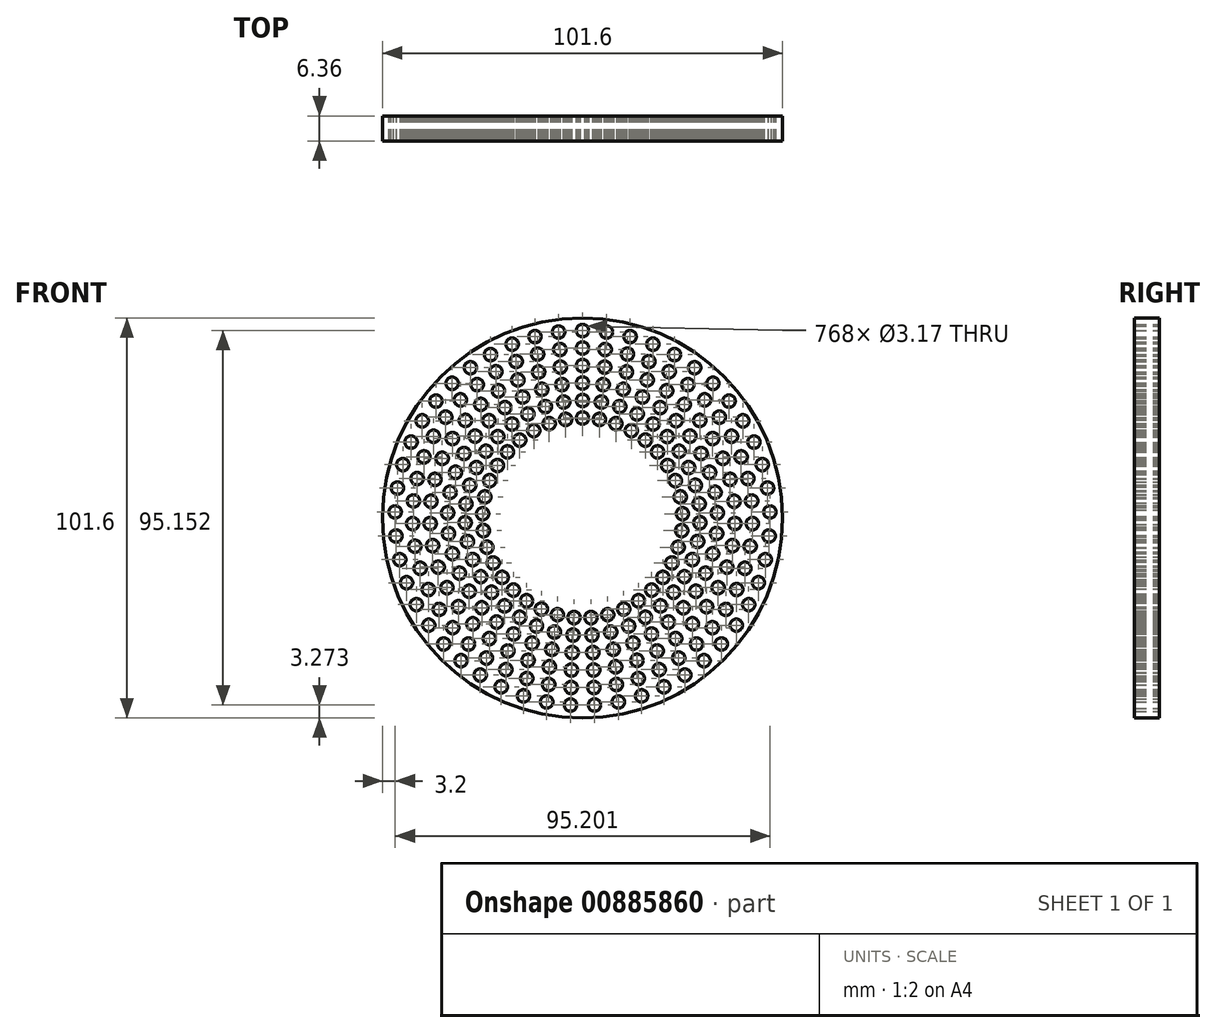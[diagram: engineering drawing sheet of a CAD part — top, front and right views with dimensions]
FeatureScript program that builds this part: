
annotation { "Feature Type Name" : "Feature", "Feature Type Description" : "" }
export const myFeature = defineFeature(function(context is Context, id is Id, definition is map)
    precondition{}
    {
        {
            var Q0;
            Q0=qCreatedBy(makeId("Front.planeOp"),FACE);
            var sketch = newSketch(context, id + "F0", { "sketchPlane" : qUnion([Q0])});
            skCircle(sketch, "E0", {"center": v(0, 0) * mm, "radius": 50.8 * mm});
            skCircle(sketch, "E1", {"center": v(0, 47.63) * mm, "radius": 1.59 * mm});
            skCircle(sketch, "E2.1.0", {"center": v(-6.1, 47.23) * mm, "radius": 1.59 * mm});
            skCircle(sketch, "E2.2.0", {"center": v(-12.08, 46.07) * mm, "radius": 1.59 * mm});
            skCircle(sketch, "E2.3.0", {"center": v(-17.87, 44.14) * mm, "radius": 1.59 * mm});
            skCircle(sketch, "E2.4.0", {"center": v(-23.37, 41.5) * mm, "radius": 1.59 * mm});
            skCircle(sketch, "E2.5.0", {"center": v(-28.49, 38.17) * mm, "radius": 1.59 * mm});
            skCircle(sketch, "E2.6.0", {"center": v(-33.13, 34.21) * mm, "radius": 1.59 * mm});
            skCircle(sketch, "E2.7.0", {"center": v(-37.23, 29.7) * mm, "radius": 1.59 * mm});
            skCircle(sketch, "E2.8.0", {"center": v(-40.73, 24.69) * mm, "radius": 1.59 * mm});
            skCircle(sketch, "E2.9.0", {"center": v(-43.55, 19.28) * mm, "radius": 1.59 * mm});
            skCircle(sketch, "E2.10.0", {"center": v(-45.66, 13.55) * mm, "radius": 1.59 * mm});
            skCircle(sketch, "E2.11.0", {"center": v(-47.01, 7.6) * mm, "radius": 1.59 * mm});
            skCircle(sketch, "E2.12.0", {"center": v(-47.6, 1.53) * mm, "radius": 1.59 * mm});
            skCircle(sketch, "E2.13.0", {"center": v(-47.4, -4.57) * mm, "radius": 1.59 * mm});
            skCircle(sketch, "E2.14.0", {"center": v(-46.43, -10.6) * mm, "radius": 1.59 * mm});
            skCircle(sketch, "E2.15.0", {"center": v(-44.7, -16.45) * mm, "radius": 1.59 * mm});
            skCircle(sketch, "E2.16.0", {"center": v(-42.22, -22.03) * mm, "radius": 1.59 * mm});
            skCircle(sketch, "E2.17.0", {"center": v(-39.06, -27.25) * mm, "radius": 1.59 * mm});
            skCircle(sketch, "E2.18.0", {"center": v(-35.26, -32.02) * mm, "radius": 1.59 * mm});
            skCircle(sketch, "E2.19.0", {"center": v(-30.87, -36.26) * mm, "radius": 1.59 * mm});
            skCircle(sketch, "E2.20.0", {"center": v(-25.98, -39.91) * mm, "radius": 1.59 * mm});
            skCircle(sketch, "E2.21.0", {"center": v(-20.66, -42.9) * mm, "radius": 1.59 * mm});
            skCircle(sketch, "E2.22.0", {"center": v(-15, -45.2) * mm, "radius": 1.59 * mm});
            skCircle(sketch, "E2.23.0", {"center": v(-9.1, -46.75) * mm, "radius": 1.59 * mm});
            skCircle(sketch, "E2.24.0", {"center": v(-3.05, -47.53) * mm, "radius": 1.59 * mm});
            skCircle(sketch, "E2.25.0", {"center": v(3.05, -47.53) * mm, "radius": 1.59 * mm});
            skCircle(sketch, "E2.26.0", {"center": v(9.1, -46.75) * mm, "radius": 1.59 * mm});
            skCircle(sketch, "E2.27.0", {"center": v(15, -45.2) * mm, "radius": 1.59 * mm});
            skCircle(sketch, "E2.28.0", {"center": v(20.66, -42.9) * mm, "radius": 1.59 * mm});
            skCircle(sketch, "E2.29.0", {"center": v(25.98, -39.91) * mm, "radius": 1.59 * mm});
            skCircle(sketch, "E2.30.0", {"center": v(30.87, -36.26) * mm, "radius": 1.59 * mm});
            skCircle(sketch, "E2.31.0", {"center": v(35.26, -32.02) * mm, "radius": 1.59 * mm});
            skCircle(sketch, "E2.32.0", {"center": v(39.06, -27.25) * mm, "radius": 1.59 * mm});
            skCircle(sketch, "E2.33.0", {"center": v(42.22, -22.03) * mm, "radius": 1.59 * mm});
            skCircle(sketch, "E2.34.0", {"center": v(44.7, -16.45) * mm, "radius": 1.59 * mm});
            skCircle(sketch, "E2.35.0", {"center": v(46.43, -10.6) * mm, "radius": 1.59 * mm});
            skCircle(sketch, "E2.36.0", {"center": v(47.4, -4.57) * mm, "radius": 1.59 * mm});
            skCircle(sketch, "E2.37.0", {"center": v(47.6, 1.53) * mm, "radius": 1.59 * mm});
            skCircle(sketch, "E2.38.0", {"center": v(47.01, 7.6) * mm, "radius": 1.59 * mm});
            skCircle(sketch, "E2.39.0", {"center": v(45.66, 13.55) * mm, "radius": 1.59 * mm});
            skCircle(sketch, "E2.40.0", {"center": v(43.55, 19.28) * mm, "radius": 1.59 * mm});
            skCircle(sketch, "E3", {"center": v(0, 43.18) * mm, "radius": 1.59 * mm});
            skCircle(sketch, "E4.1.0", {"center": v(-5.76, 42.8) * mm, "radius": 1.59 * mm});
            skCircle(sketch, "E4.2.0", {"center": v(-11.4, 41.65) * mm, "radius": 1.59 * mm});
            skCircle(sketch, "E4.3.0", {"center": v(-16.86, 39.75) * mm, "radius": 1.59 * mm});
            skCircle(sketch, "E4.4.0", {"center": v(-22, 37.15) * mm, "radius": 1.59 * mm});
            skCircle(sketch, "E4.5.0", {"center": v(-26.76, 33.89) * mm, "radius": 1.59 * mm});
            skCircle(sketch, "E4.6.0", {"center": v(-31.04, 30.02) * mm, "radius": 1.59 * mm});
            skCircle(sketch, "E4.7.0", {"center": v(-34.76, 25.61) * mm, "radius": 1.59 * mm});
            skCircle(sketch, "E4.8.0", {"center": v(-37.87, 20.75) * mm, "radius": 1.59 * mm});
            skCircle(sketch, "E4.9.0", {"center": v(-40.3, 15.52) * mm, "radius": 1.59 * mm});
            skCircle(sketch, "E4.10.0", {"center": v(-42, 10) * mm, "radius": 1.59 * mm});
            skCircle(sketch, "E4.11.0", {"center": v(-42.96, 4.32) * mm, "radius": 1.59 * mm});
            skCircle(sketch, "E4.12.0", {"center": v(-43.16, -1.44) * mm, "radius": 1.59 * mm});
            skCircle(sketch, "E4.13.0", {"center": v(-42.58, -7.18) * mm, "radius": 1.59 * mm});
            skCircle(sketch, "E4.14.0", {"center": v(-41.24, -12.8) * mm, "radius": 1.59 * mm});
            skCircle(sketch, "E4.15.0", {"center": v(-39.17, -18.18) * mm, "radius": 1.59 * mm});
            skCircle(sketch, "E4.16.0", {"center": v(-36.4, -23.23) * mm, "radius": 1.59 * mm});
            skCircle(sketch, "E4.17.0", {"center": v(-32.97, -27.88) * mm, "radius": 1.59 * mm});
            skCircle(sketch, "E4.18.0", {"center": v(-28.96, -32.02) * mm, "radius": 1.59 * mm});
            skCircle(sketch, "E4.19.0", {"center": v(-24.44, -35.6) * mm, "radius": 1.59 * mm});
            skCircle(sketch, "E4.20.0", {"center": v(-19.47, -38.54) * mm, "radius": 1.59 * mm});
            skCircle(sketch, "E4.21.0", {"center": v(-14.16, -40.8) * mm, "radius": 1.59 * mm});
            skCircle(sketch, "E4.22.0", {"center": v(-8.6, -42.31) * mm, "radius": 1.59 * mm});
            skCircle(sketch, "E4.23.0", {"center": v(-2.88, -43.08) * mm, "radius": 1.59 * mm});
            skCircle(sketch, "E4.24.0", {"center": v(2.88, -43.08) * mm, "radius": 1.59 * mm});
            skCircle(sketch, "E4.25.0", {"center": v(8.6, -42.31) * mm, "radius": 1.59 * mm});
            skCircle(sketch, "E4.26.0", {"center": v(14.16, -40.8) * mm, "radius": 1.59 * mm});
            skCircle(sketch, "E4.27.0", {"center": v(19.47, -38.54) * mm, "radius": 1.59 * mm});
            skCircle(sketch, "E4.28.0", {"center": v(24.44, -35.6) * mm, "radius": 1.59 * mm});
            skCircle(sketch, "E4.29.0", {"center": v(28.96, -32.02) * mm, "radius": 1.59 * mm});
            skCircle(sketch, "E4.30.0", {"center": v(32.97, -27.88) * mm, "radius": 1.59 * mm});
            skCircle(sketch, "E4.31.0", {"center": v(36.4, -23.23) * mm, "radius": 1.59 * mm});
            skCircle(sketch, "E4.32.0", {"center": v(39.17, -18.18) * mm, "radius": 1.59 * mm});
            skCircle(sketch, "E4.33.0", {"center": v(41.24, -12.8) * mm, "radius": 1.59 * mm});
            skCircle(sketch, "E4.34.0", {"center": v(42.58, -7.18) * mm, "radius": 1.59 * mm});
            skCircle(sketch, "E4.35.0", {"center": v(43.16, -1.44) * mm, "radius": 1.59 * mm});
            skCircle(sketch, "E4.36.0", {"center": v(42.96, 4.32) * mm, "radius": 1.59 * mm});
            skCircle(sketch, "E4.37.0", {"center": v(42, 10) * mm, "radius": 1.59 * mm});
            skCircle(sketch, "E4.38.0", {"center": v(40.3, 15.52) * mm, "radius": 1.59 * mm});
            skCircle(sketch, "E5.1.41.0", {"center": v(40.73, 24.69) * mm, "radius": 1.59 * mm});
            skCircle(sketch, "E5.1.42.0", {"center": v(37.23, 29.7) * mm, "radius": 1.59 * mm});
            skCircle(sketch, "E5.1.43.0", {"center": v(33.13, 34.21) * mm, "radius": 1.59 * mm});
            skCircle(sketch, "E5.1.44.0", {"center": v(28.49, 38.17) * mm, "radius": 1.59 * mm});
            skCircle(sketch, "E5.1.45.0", {"center": v(23.37, 41.5) * mm, "radius": 1.59 * mm});
            skCircle(sketch, "E5.1.46.0", {"center": v(17.87, 44.14) * mm, "radius": 1.59 * mm});
            skCircle(sketch, "E5.1.47.0", {"center": v(12.08, 46.07) * mm, "radius": 1.59 * mm});
            skCircle(sketch, "E5.1.48.0", {"center": v(6.1, 47.23) * mm, "radius": 1.59 * mm});
            skCircle(sketch, "E6.1.39.0", {"center": v(37.87, 20.75) * mm, "radius": 1.59 * mm});
            skCircle(sketch, "E6.1.40.0", {"center": v(34.76, 25.61) * mm, "radius": 1.59 * mm});
            skCircle(sketch, "E6.1.41.0", {"center": v(31.04, 30.02) * mm, "radius": 1.59 * mm});
            skCircle(sketch, "E6.1.42.0", {"center": v(26.76, 33.89) * mm, "radius": 1.59 * mm});
            skCircle(sketch, "E6.1.43.0", {"center": v(22, 37.15) * mm, "radius": 1.59 * mm});
            skCircle(sketch, "E6.1.44.0", {"center": v(16.86, 39.75) * mm, "radius": 1.59 * mm});
            skCircle(sketch, "E6.1.45.0", {"center": v(11.4, 41.65) * mm, "radius": 1.59 * mm});
            skCircle(sketch, "E6.1.46.0", {"center": v(5.76, 42.8) * mm, "radius": 1.59 * mm});
            skCircle(sketch, "E7", {"center": v(0, 38.74) * mm, "radius": 1.59 * mm});
            skCircle(sketch, "E8.1.0", {"center": v(-5.64, 38.32) * mm, "radius": 1.59 * mm});
            skCircle(sketch, "E8.2.0", {"center": v(-11.16, 37.1) * mm, "radius": 1.59 * mm});
            skCircle(sketch, "E8.3.0", {"center": v(-16.44, 35.07) * mm, "radius": 1.59 * mm});
            skCircle(sketch, "E8.4.0", {"center": v(-21.37, 32.3) * mm, "radius": 1.59 * mm});
            skCircle(sketch, "E8.5.0", {"center": v(-25.85, 28.85) * mm, "radius": 1.59 * mm});
            skCircle(sketch, "E8.6.0", {"center": v(-29.77, 24.78) * mm, "radius": 1.59 * mm});
            skCircle(sketch, "E8.7.0", {"center": v(-33.06, 20.18) * mm, "radius": 1.59 * mm});
            skCircle(sketch, "E8.8.0", {"center": v(-35.65, 15.15) * mm, "radius": 1.59 * mm});
            skCircle(sketch, "E8.9.0", {"center": v(-37.48, 9.8) * mm, "radius": 1.59 * mm});
            skCircle(sketch, "E8.10.0", {"center": v(-38.5, 4.24) * mm, "radius": 1.59 * mm});
            skCircle(sketch, "E8.11.0", {"center": v(-38.7, -1.41) * mm, "radius": 1.59 * mm});
            skCircle(sketch, "E8.12.0", {"center": v(-38.1, -7.04) * mm, "radius": 1.59 * mm});
            skCircle(sketch, "E8.13.0", {"center": v(-36.66, -12.5) * mm, "radius": 1.59 * mm});
            skCircle(sketch, "E8.14.0", {"center": v(-34.45, -17.71) * mm, "radius": 1.59 * mm});
            skCircle(sketch, "E8.15.0", {"center": v(-31.5, -22.54) * mm, "radius": 1.59 * mm});
            skCircle(sketch, "E8.16.0", {"center": v(-27.89, -26.88) * mm, "radius": 1.59 * mm});
            skCircle(sketch, "E8.17.0", {"center": v(-23.67, -30.66) * mm, "radius": 1.59 * mm});
            skCircle(sketch, "E8.18.0", {"center": v(-18.96, -33.78) * mm, "radius": 1.59 * mm});
            skCircle(sketch, "E8.19.0", {"center": v(-13.84, -36.18) * mm, "radius": 1.59 * mm});
            skCircle(sketch, "E8.20.0", {"center": v(-8.42, -37.8) * mm, "radius": 1.59 * mm});
            skCircle(sketch, "E8.21.0", {"center": v(-2.83, -38.63) * mm, "radius": 1.59 * mm});
            skCircle(sketch, "E8.22.0", {"center": v(2.83, -38.63) * mm, "radius": 1.59 * mm});
            skCircle(sketch, "E8.23.0", {"center": v(8.42, -37.8) * mm, "radius": 1.59 * mm});
            skCircle(sketch, "E8.24.0", {"center": v(13.84, -36.18) * mm, "radius": 1.59 * mm});
            skCircle(sketch, "E8.25.0", {"center": v(18.96, -33.78) * mm, "radius": 1.59 * mm});
            skCircle(sketch, "E8.26.0", {"center": v(23.67, -30.66) * mm, "radius": 1.59 * mm});
            skCircle(sketch, "E8.27.0", {"center": v(27.89, -26.88) * mm, "radius": 1.59 * mm});
            skCircle(sketch, "E8.28.0", {"center": v(31.5, -22.54) * mm, "radius": 1.59 * mm});
            skCircle(sketch, "E8.29.0", {"center": v(34.45, -17.71) * mm, "radius": 1.59 * mm});
            skCircle(sketch, "E8.30.0", {"center": v(36.66, -12.5) * mm, "radius": 1.59 * mm});
            skCircle(sketch, "E8.31.0", {"center": v(38.1, -7.04) * mm, "radius": 1.59 * mm});
            skCircle(sketch, "E8.32.0", {"center": v(38.7, -1.41) * mm, "radius": 1.59 * mm});
            skCircle(sketch, "E8.33.0", {"center": v(38.5, 4.24) * mm, "radius": 1.59 * mm});
            skCircle(sketch, "E8.34.0", {"center": v(37.48, 9.8) * mm, "radius": 1.59 * mm});
            skCircle(sketch, "E8.35.0", {"center": v(35.65, 15.15) * mm, "radius": 1.59 * mm});
            skCircle(sketch, "E8.36.0", {"center": v(33.06, 20.18) * mm, "radius": 1.59 * mm});
            skCircle(sketch, "E8.37.0", {"center": v(29.77, 24.78) * mm, "radius": 1.59 * mm});
            skCircle(sketch, "E8.38.0", {"center": v(25.85, 28.85) * mm, "radius": 1.59 * mm});
            skCircle(sketch, "E8.39.0", {"center": v(21.37, 32.3) * mm, "radius": 1.59 * mm});
            skCircle(sketch, "E8.40.0", {"center": v(16.44, 35.07) * mm, "radius": 1.59 * mm});
            skCircle(sketch, "E8.41.0", {"center": v(11.16, 37.1) * mm, "radius": 1.59 * mm});
            skCircle(sketch, "E8.42.0", {"center": v(5.64, 38.32) * mm, "radius": 1.59 * mm});
            skCircle(sketch, "E9", {"center": v(0, 34.3) * mm, "radius": 1.59 * mm});
            skCircle(sketch, "E10.1.0", {"center": v(-5.23, 33.89) * mm, "radius": 1.59 * mm});
            skCircle(sketch, "E10.2.0", {"center": v(-10.35, 32.7) * mm, "radius": 1.59 * mm});
            skCircle(sketch, "E10.3.0", {"center": v(-15.22, 30.73) * mm, "radius": 1.59 * mm});
            skCircle(sketch, "E10.4.0", {"center": v(-19.73, 28.05) * mm, "radius": 1.59 * mm});
            skCircle(sketch, "E10.5.0", {"center": v(-23.78, 24.7) * mm, "radius": 1.59 * mm});
            skCircle(sketch, "E10.6.0", {"center": v(-27.27, 20.79) * mm, "radius": 1.59 * mm});
            skCircle(sketch, "E10.7.0", {"center": v(-30.12, 16.38) * mm, "radius": 1.59 * mm});
            skCircle(sketch, "E10.8.0", {"center": v(-32.27, 11.6) * mm, "radius": 1.59 * mm});
            skCircle(sketch, "E10.9.0", {"center": v(-33.66, 6.53) * mm, "radius": 1.59 * mm});
            skCircle(sketch, "E10.10.0", {"center": v(-34.26, 1.31) * mm, "radius": 1.59 * mm});
            skCircle(sketch, "E10.11.0", {"center": v(-34.06, -3.93) * mm, "radius": 1.59 * mm});
            skCircle(sketch, "E10.12.0", {"center": v(-33.06, -9.09) * mm, "radius": 1.59 * mm});
            skCircle(sketch, "E10.13.0", {"center": v(-31.29, -14.03) * mm, "radius": 1.59 * mm});
            skCircle(sketch, "E10.14.0", {"center": v(-28.78, -18.64) * mm, "radius": 1.59 * mm});
            skCircle(sketch, "E10.15.0", {"center": v(-25.6, -22.81) * mm, "radius": 1.59 * mm});
            skCircle(sketch, "E10.16.0", {"center": v(-21.82, -26.45) * mm, "radius": 1.59 * mm});
            skCircle(sketch, "E10.17.0", {"center": v(-17.52, -29.47) * mm, "radius": 1.59 * mm});
            skCircle(sketch, "E10.18.0", {"center": v(-12.82, -31.8) * mm, "radius": 1.59 * mm});
            skCircle(sketch, "E10.19.0", {"center": v(-7.81, -33.39) * mm, "radius": 1.59 * mm});
            skCircle(sketch, "E10.20.0", {"center": v(-2.62, -34.19) * mm, "radius": 1.59 * mm});
            skCircle(sketch, "E10.21.0", {"center": v(2.62, -34.19) * mm, "radius": 1.59 * mm});
            skCircle(sketch, "E10.22.0", {"center": v(7.81, -33.39) * mm, "radius": 1.59 * mm});
            skCircle(sketch, "E10.23.0", {"center": v(12.82, -31.8) * mm, "radius": 1.59 * mm});
            skCircle(sketch, "E10.24.0", {"center": v(17.52, -29.47) * mm, "radius": 1.59 * mm});
            skCircle(sketch, "E10.25.0", {"center": v(21.82, -26.45) * mm, "radius": 1.59 * mm});
            skCircle(sketch, "E10.26.0", {"center": v(25.6, -22.81) * mm, "radius": 1.59 * mm});
            skCircle(sketch, "E10.27.0", {"center": v(28.78, -18.64) * mm, "radius": 1.59 * mm});
            skCircle(sketch, "E10.28.0", {"center": v(31.29, -14.03) * mm, "radius": 1.59 * mm});
            skCircle(sketch, "E10.29.0", {"center": v(33.06, -9.09) * mm, "radius": 1.59 * mm});
            skCircle(sketch, "E10.30.0", {"center": v(34.06, -3.93) * mm, "radius": 1.59 * mm});
            skCircle(sketch, "E10.31.0", {"center": v(34.26, 1.31) * mm, "radius": 1.59 * mm});
            skCircle(sketch, "E10.32.0", {"center": v(33.66, 6.53) * mm, "radius": 1.59 * mm});
            skCircle(sketch, "E10.33.0", {"center": v(32.27, 11.6) * mm, "radius": 1.59 * mm});
            skCircle(sketch, "E10.34.0", {"center": v(30.12, 16.38) * mm, "radius": 1.59 * mm});
            skCircle(sketch, "E10.35.0", {"center": v(27.27, 20.79) * mm, "radius": 1.59 * mm});
            skCircle(sketch, "E10.36.0", {"center": v(23.78, 24.7) * mm, "radius": 1.59 * mm});
            skCircle(sketch, "E10.37.0", {"center": v(19.73, 28.05) * mm, "radius": 1.59 * mm});
            skCircle(sketch, "E10.38.0", {"center": v(15.22, 30.73) * mm, "radius": 1.59 * mm});
            skCircle(sketch, "E10.39.0", {"center": v(10.35, 32.7) * mm, "radius": 1.59 * mm});
            skCircle(sketch, "E10.40.0", {"center": v(5.23, 33.89) * mm, "radius": 1.59 * mm});
            skCircle(sketch, "E11", {"center": v(0, 29.85) * mm, "radius": 1.59 * mm});
            skCircle(sketch, "E12.1.0", {"center": v(-4.79, 29.46) * mm, "radius": 1.59 * mm});
            skCircle(sketch, "E12.2.0", {"center": v(-9.45, 28.3) * mm, "radius": 1.59 * mm});
            skCircle(sketch, "E12.3.0", {"center": v(-13.87, 26.43) * mm, "radius": 1.59 * mm});
            skCircle(sketch, "E12.4.0", {"center": v(-17.93, 23.86) * mm, "radius": 1.59 * mm});
            skCircle(sketch, "E12.5.0", {"center": v(-21.52, 20.67) * mm, "radius": 1.59 * mm});
            skCircle(sketch, "E12.6.0", {"center": v(-24.56, 16.95) * mm, "radius": 1.59 * mm});
            skCircle(sketch, "E12.7.0", {"center": v(-26.96, 12.8) * mm, "radius": 1.59 * mm});
            skCircle(sketch, "E12.8.0", {"center": v(-28.67, 8.3) * mm, "radius": 1.59 * mm});
            skCircle(sketch, "E12.9.0", {"center": v(-29.63, 3.6) * mm, "radius": 1.59 * mm});
            skCircle(sketch, "E12.10.0", {"center": v(-29.82, -1.2) * mm, "radius": 1.59 * mm});
            skCircle(sketch, "E12.11.0", {"center": v(-29.24, -5.97) * mm, "radius": 1.59 * mm});
            skCircle(sketch, "E12.12.0", {"center": v(-27.9, -10.58) * mm, "radius": 1.59 * mm});
            skCircle(sketch, "E12.13.0", {"center": v(-25.85, -14.92) * mm, "radius": 1.59 * mm});
            skCircle(sketch, "E12.14.0", {"center": v(-23.12, -18.88) * mm, "radius": 1.59 * mm});
            skCircle(sketch, "E12.15.0", {"center": v(-19.8, -22.34) * mm, "radius": 1.59 * mm});
            skCircle(sketch, "E12.16.0", {"center": v(-15.95, -25.22) * mm, "radius": 1.59 * mm});
            skCircle(sketch, "E12.17.0", {"center": v(-11.7, -27.46) * mm, "radius": 1.59 * mm});
            skCircle(sketch, "E12.18.0", {"center": v(-7.14, -28.98) * mm, "radius": 1.59 * mm});
            skCircle(sketch, "E12.19.0", {"center": v(-2.4, -29.75) * mm, "radius": 1.59 * mm});
            skCircle(sketch, "E12.20.0", {"center": v(2.4, -29.75) * mm, "radius": 1.59 * mm});
            skCircle(sketch, "E12.21.0", {"center": v(7.14, -28.98) * mm, "radius": 1.59 * mm});
            skCircle(sketch, "E12.22.0", {"center": v(11.7, -27.46) * mm, "radius": 1.59 * mm});
            skCircle(sketch, "E12.23.0", {"center": v(15.95, -25.22) * mm, "radius": 1.59 * mm});
            skCircle(sketch, "E12.24.0", {"center": v(19.8, -22.34) * mm, "radius": 1.59 * mm});
            skCircle(sketch, "E12.25.0", {"center": v(23.12, -18.88) * mm, "radius": 1.59 * mm});
            skCircle(sketch, "E12.26.0", {"center": v(25.85, -14.92) * mm, "radius": 1.59 * mm});
            skCircle(sketch, "E12.27.0", {"center": v(27.9, -10.58) * mm, "radius": 1.59 * mm});
            skCircle(sketch, "E12.28.0", {"center": v(29.24, -5.97) * mm, "radius": 1.59 * mm});
            skCircle(sketch, "E12.29.0", {"center": v(29.82, -1.2) * mm, "radius": 1.59 * mm});
            skCircle(sketch, "E12.30.0", {"center": v(29.63, 3.6) * mm, "radius": 1.59 * mm});
            skCircle(sketch, "E12.31.0", {"center": v(28.67, 8.3) * mm, "radius": 1.59 * mm});
            skCircle(sketch, "E12.32.0", {"center": v(26.96, 12.8) * mm, "radius": 1.59 * mm});
            skCircle(sketch, "E12.33.0", {"center": v(24.56, 16.95) * mm, "radius": 1.59 * mm});
            skCircle(sketch, "E12.34.0", {"center": v(21.52, 20.67) * mm, "radius": 1.59 * mm});
            skCircle(sketch, "E12.35.0", {"center": v(17.93, 23.86) * mm, "radius": 1.59 * mm});
            skCircle(sketch, "E12.36.0", {"center": v(13.87, 26.43) * mm, "radius": 1.59 * mm});
            skCircle(sketch, "E12.37.0", {"center": v(9.45, 28.3) * mm, "radius": 1.59 * mm});
            skCircle(sketch, "E12.38.0", {"center": v(4.79, 29.46) * mm, "radius": 1.59 * mm});
            skCircle(sketch, "E13", {"center": v(0, 25.4) * mm, "radius": 1.59 * mm});
            skCircle(sketch, "E14.1.0", {"center": v(-4.3, 25.03) * mm, "radius": 1.59 * mm});
            skCircle(sketch, "E14.2.0", {"center": v(-8.46, 23.95) * mm, "radius": 1.59 * mm});
            skCircle(sketch, "E14.3.0", {"center": v(-12.39, 22.17) * mm, "radius": 1.59 * mm});
            skCircle(sketch, "E14.4.0", {"center": v(-15.96, 19.76) * mm, "radius": 1.59 * mm});
            skCircle(sketch, "E14.5.0", {"center": v(-19.07, 16.78) * mm, "radius": 1.59 * mm});
            skCircle(sketch, "E14.6.0", {"center": v(-21.63, 13.32) * mm, "radius": 1.59 * mm});
            skCircle(sketch, "E14.7.0", {"center": v(-23.57, 9.47) * mm, "radius": 1.59 * mm});
            skCircle(sketch, "E14.8.0", {"center": v(-24.83, 5.35) * mm, "radius": 1.59 * mm});
            skCircle(sketch, "E14.9.0", {"center": v(-25.38, 1.08) * mm, "radius": 1.59 * mm});
            skCircle(sketch, "E14.10.0", {"center": v(-25.2, -3.23) * mm, "radius": 1.59 * mm});
            skCircle(sketch, "E14.11.0", {"center": v(-24.29, -7.44) * mm, "radius": 1.59 * mm});
            skCircle(sketch, "E14.12.0", {"center": v(-22.68, -11.44) * mm, "radius": 1.59 * mm});
            skCircle(sketch, "E14.13.0", {"center": v(-20.42, -15.1) * mm, "radius": 1.59 * mm});
            skCircle(sketch, "E14.14.0", {"center": v(-17.58, -18.34) * mm, "radius": 1.59 * mm});
            skCircle(sketch, "E14.15.0", {"center": v(-14.22, -21.04) * mm, "radius": 1.59 * mm});
            skCircle(sketch, "E14.16.0", {"center": v(-10.46, -23.15) * mm, "radius": 1.59 * mm});
            skCircle(sketch, "E14.17.0", {"center": v(-6.4, -24.58) * mm, "radius": 1.59 * mm});
            skCircle(sketch, "E14.18.0", {"center": v(-2.15, -25.3) * mm, "radius": 1.59 * mm});
            skCircle(sketch, "E14.19.0", {"center": v(2.15, -25.3) * mm, "radius": 1.59 * mm});
            skCircle(sketch, "E14.20.0", {"center": v(6.4, -24.58) * mm, "radius": 1.59 * mm});
            skCircle(sketch, "E14.21.0", {"center": v(10.46, -23.15) * mm, "radius": 1.59 * mm});
            skCircle(sketch, "E14.22.0", {"center": v(14.22, -21.04) * mm, "radius": 1.59 * mm});
            skCircle(sketch, "E14.23.0", {"center": v(17.58, -18.34) * mm, "radius": 1.59 * mm});
            skCircle(sketch, "E14.24.0", {"center": v(20.42, -15.1) * mm, "radius": 1.59 * mm});
            skCircle(sketch, "E14.25.0", {"center": v(22.68, -11.44) * mm, "radius": 1.59 * mm});
            skCircle(sketch, "E14.26.0", {"center": v(24.29, -7.44) * mm, "radius": 1.59 * mm});
            skCircle(sketch, "E14.27.0", {"center": v(25.2, -3.23) * mm, "radius": 1.59 * mm});
            skCircle(sketch, "E14.28.0", {"center": v(25.38, 1.08) * mm, "radius": 1.59 * mm});
            skCircle(sketch, "E14.29.0", {"center": v(24.83, 5.35) * mm, "radius": 1.59 * mm});
            skCircle(sketch, "E14.30.0", {"center": v(23.57, 9.47) * mm, "radius": 1.59 * mm});
            skCircle(sketch, "E14.31.0", {"center": v(21.63, 13.32) * mm, "radius": 1.59 * mm});
            skCircle(sketch, "E14.32.0", {"center": v(19.07, 16.78) * mm, "radius": 1.59 * mm});
            skCircle(sketch, "E14.33.0", {"center": v(15.96, 19.76) * mm, "radius": 1.59 * mm});
            skCircle(sketch, "E14.34.0", {"center": v(12.39, 22.17) * mm, "radius": 1.59 * mm});
            skCircle(sketch, "E14.35.0", {"center": v(8.46, 23.95) * mm, "radius": 1.59 * mm});
            skCircle(sketch, "E14.36.0", {"center": v(4.3, 25.03) * mm, "radius": 1.59 * mm});
            skSolve(sketch);
        }
        {
            var Q0;
            Q0=makeQuery(id+"F0.imprint","IMPRINT",FACE,{"disambiguationData":[TD([[makeQuery(id+"F0.imprint","IMPRINT",EDGE,{"derivedFrom":sQuery(id+"F0.wireOp",EDGE,"E0")}),1.0]])]});
            extrude(context, id + "F1", {"entities" : qUnion([Q0]), "endBound" : BoundingType.SYMMETRIC, "depth" : 6.35 * mm, "offsetDistance" : 25.4 * mm});
        }
    });
